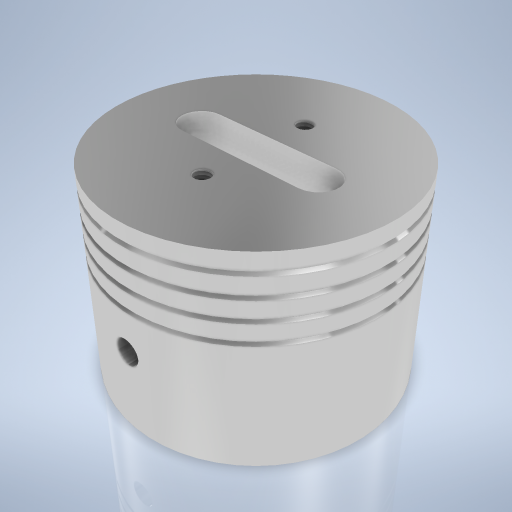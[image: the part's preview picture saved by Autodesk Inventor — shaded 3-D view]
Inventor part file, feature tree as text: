
AUTODESK INVENTOR PART (.ipt)
format: ipt  version: 2024.2 (Build 282272000, 272)  size: 333,312 bytes
history: native  units: mm
features: sketch x5, hole x3, revolve x1, extrude x1, plane x1
ambient origin geometry x8: Origin, YZ Plane, XZ Plane, XY Plane, X Axis, Y Axis, Z Axis, Center Point
bodies: Volumenkörper1 (feature_tree)
feature tree (11):
  revolve  "Umdrehung1"
  hole  "Bohrung1"  [1 undecoded]
  extrude  "Extrusion1"  Depth=6.0mm
  hole  "Bohrung2"  [1 undecoded]
  plane  "Arbeitsebene1"
  hole  "Bohrung3"  [1 undecoded]
  sketch  "Skizze1"  dims[d0=0.75mm d1=90.0deg]
  sketch  "Skizze2"  dims[d2=5.25mm d3=6.0mm]
  sketch  "Skizze3"  dims[d4=6.0mm d5=6.0mm]
  sketch  "Skizze4"  dims[d6=60.0mm d7=82.0mm]
  sketch  "Skizze5"  dims[d8=360.0deg d9=20.0mm d10=6.0mm d11=63.75mm d12=12.0mm d13=90.0deg d14=30.0mm d15=20.594885mm d16=49.5mm d17=12.0mm d18=10.0mm d19=0.0mm d20=16.5mm d21=16.5mm d22=4.917mm d23=12.0mm d24=51.0mm d25=12.0mm d26=90.0deg d27=20.25mm d28=20.594885mm d29=50.0mm d30=24.0mm d31=7.5mm d32=12.0mm d33=4.0mm d34=2.0mm d35=90.0deg d36=20.25mm d37=20.594885mm]
note: 3 required parameter values undecoded (feature->parameter linkage not recoverable at this tier; creation-order binding heuristic only, values carry confidence <= 0.55)
